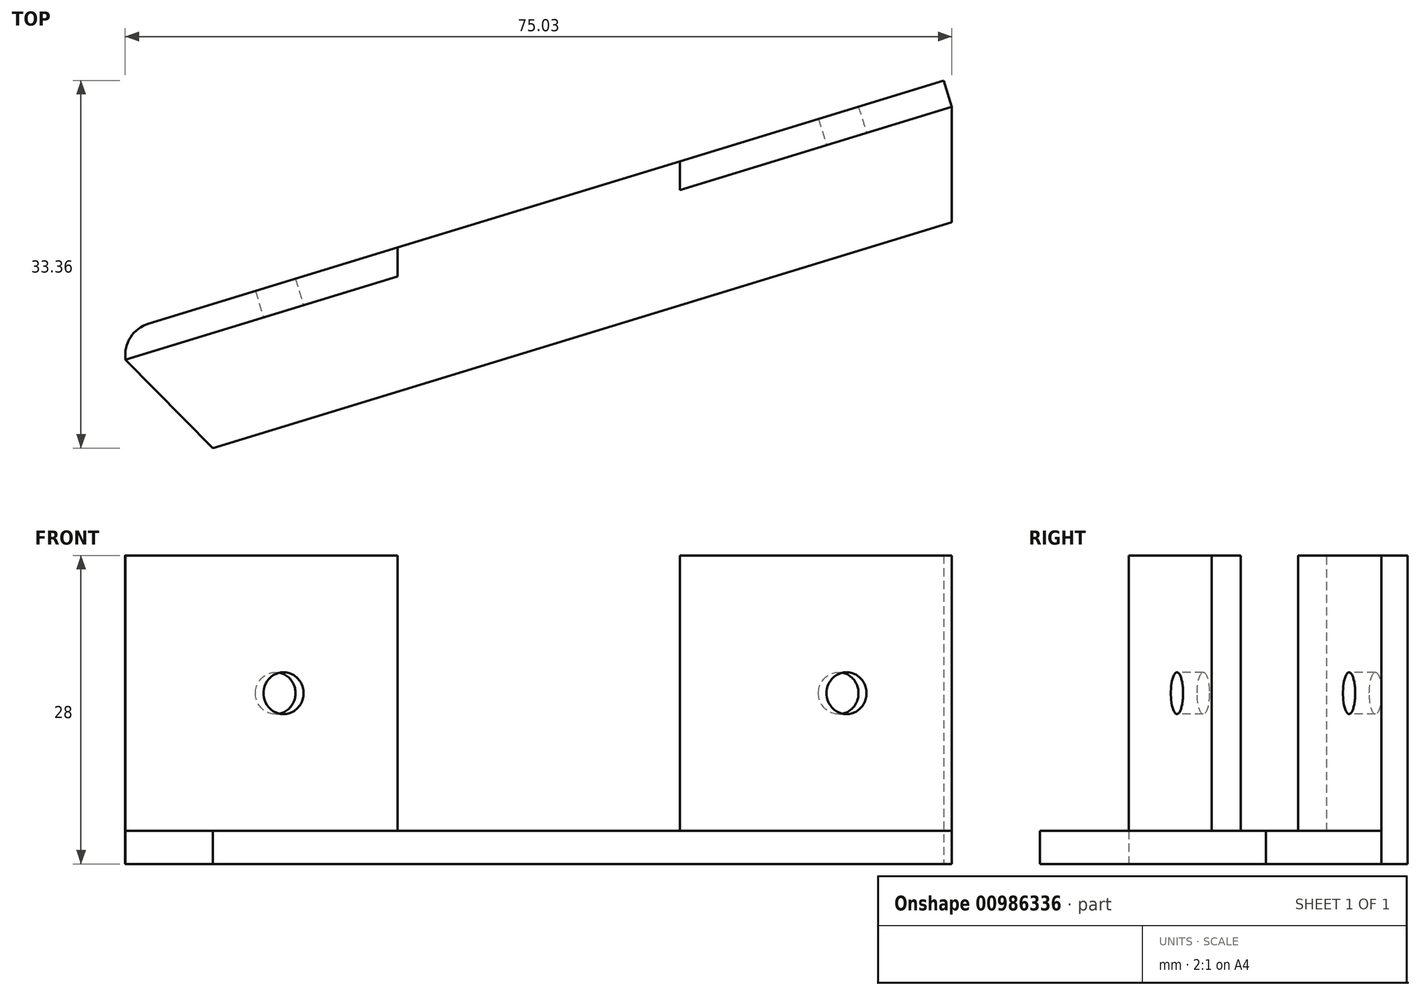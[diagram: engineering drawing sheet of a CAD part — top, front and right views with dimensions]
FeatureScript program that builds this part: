
annotation { "Feature Type Name" : "Feature", "Feature Type Description" : "" }
export const myFeature = defineFeature(function(context is Context, id is Id, definition is map)
    precondition{}
    {
        {
            var Q0;
            Q0=qCreatedBy(makeId("Top.planeOp"),FACE);
            var sketch = newSketch(context, id + "F0", { "sketchPlane" : qUnion([Q0])});
            skLineSegment(sketch, "E0.bottom", {"start": v(0, 0) * mm, "end": v(50, 0) * mm});
            skLineSegment(sketch, "E0.top", {"start": v(0, 33) * mm, "end": v(50, 33) * mm});
            skLineSegment(sketch, "E0.left", {"start": v(0, 0) * mm, "end": v(0, 33) * mm});
            skLineSegment(sketch, "E0.right", {"start": v(50, 0) * mm, "end": v(50, 33) * mm});
            skLineSegment(sketch, "E1", {"start": v(0, 33) * mm, "end": v(50, 48.29) * mm});
            skLineSegment(sketch, "E2", {"start": v(50, 33) * mm, "end": v(50, 48.29) * mm});
            skLineSegment(sketch, "E3", {"start": v(0, 33) * mm, "end": v(-25, 25.36) * mm});
            skLineSegment(sketch, "E4", {"start": v(-25, 25.36) * mm, "end": v(0, 0) * mm});
            skLineSegment(sketch, "E5", {"start": v(0, 33) * mm, "end": v(0, 137) * mm});
            skLineSegment(sketch, "E6", {"start": v(0, 137) * mm, "end": v(25, 137) * mm});
            skLineSegment(sketch, "E7", {"start": v(25, 137) * mm, "end": v(25, 0) * mm});
            skLineSegment(sketch, "E8", {"start": v(0, 137) * mm, "end": v(-25, 131.69) * mm});
            skLineSegment(sketch, "E9", {"start": v(-25, 131.69) * mm, "end": v(-25, 92.43) * mm});
            skLineSegment(sketch, "E10", {"start": v(-25, 131.69) * mm, "end": v(0, 101.46) * mm});
            skLineSegment(sketch, "E11", {"start": v(0, 137) * mm, "end": v(50, 147.63) * mm});
            skLineSegment(sketch, "E12", {"start": v(50, 147.63) * mm, "end": v(50, 131.69) * mm});
            skLineSegment(sketch, "E13", {"start": v(25, 101.46) * mm, "end": v(50, 131.69) * mm});
            skLineSegment(sketch, "E14", {"start": v(0, 137) * mm, "end": v(0, 177) * mm});
            skLineSegment(sketch, "E15", {"start": v(0, 177) * mm, "end": v(25, 177) * mm});
            skPoint(sketch, "E15.endSnap0", {"position": v(25, 142.31) * mm});
            skLineSegment(sketch, "E16", {"start": v(25, 177) * mm, "end": v(25, 137) * mm});
            skSolve(sketch);
        }
        {
            var Q0;
            Q0=qSketchRegion(id+"F0",true);
            extrude(context, id + "F1", {"entities" : qUnion([Q0]), "depth" : 25 * mm});
        }
        {
            var Q0;
            Q0=makeQuery(id+"F1.opExtrude","CAP_FACE",FACE,{"disambiguationData":[OSD([sQuery(id+"F0.wireOp",EDGE,"E0.bottom"),sQuery(id+"F0.wireOp",EDGE,"E0.right"),sQuery(id+"F0.wireOp",EDGE,"E1"),sQuery(id+"F0.wireOp",EDGE,"E2"),sQuery(id+"F0.wireOp",EDGE,"E3"),sQuery(id+"F0.wireOp",EDGE,"E4"),sQuery(id+"F0.wireOp",EDGE,"E5"),sQuery(id+"F0.wireOp",EDGE,"E7"),sQuery(id+"F0.wireOp",EDGE,"E8"),sQuery(id+"F0.wireOp",EDGE,"E10"),sQuery(id+"F0.wireOp",EDGE,"E11"),sQuery(id+"F0.wireOp",EDGE,"E12"),sQuery(id+"F0.wireOp",EDGE,"E13"),sQuery(id+"F0.wireOp",EDGE,"E14"),sQuery(id+"F0.wireOp",EDGE,"E15"),sQuery(id+"F0.wireOp",EDGE,"E16")])],"isStart":true});
            var sketch = newSketch(context, id + "F2", { "sketchPlane" : qUnion([Q0])});
            skLineSegment(sketch, "E17", {"start": v(25, -101.46) * mm, "end": v(0, -101.46) * mm});
            skLineSegment(sketch, "E18", {"start": v(0, -101.46) * mm, "end": v(-25, -131.69) * mm});
            skLineSegment(sketch, "E19", {"start": v(-25, -131.69) * mm, "end": v(50, -147.63) * mm});
            skLineSegment(sketch, "E20", {"start": v(50, -147.63) * mm, "end": v(50, -131.69) * mm});
            skLineSegment(sketch, "E21", {"start": v(50, -131.69) * mm, "end": v(25, -101.46) * mm});
            skSolve(sketch);
        }
        {
            var Q0;
            Q0=qSketchRegion(id+"F2",true);
            extrude(context, id + "F3", {"entities" : qUnion([Q0]), "operationType" : NewBodyOperationType.ADD, "depth" : 10 * mm});
        }
        {
            var Q0;
            Q0=makeQuery(id+"F1.opExtrude","SWEPT_FACE",FACE,{"disambiguationData":[OSD([sQuery(id+"F0.wireOp",EDGE,"E7")])]});
            var sketch = newSketch(context, id + "F4", { "sketchPlane" : qUnion([Q0])});
            skLineSegment(sketch, "E22", {"start": v(147.63, -10) * mm, "end": v(101.46, 0) * mm});
            skLineSegment(sketch, "E23", {"start": v(101.46, 0) * mm, "end": v(101.46, -21.14) * mm});
            skLineSegment(sketch, "E24", {"start": v(101.46, -21.14) * mm, "end": v(147.63, -10) * mm});
            skSolve(sketch);
        }
        {
            var Q0;
            Q0=qSketchRegion(id+"F4",true);
            extrude(context, id + "F5", {"entities" : qUnion([Q0]), "operationType" : NewBodyOperationType.REMOVE, "oppositeDirection" : true, "depth" : 163.4 * mm, "symmetric" : true});
        }
        {
            var Q0;
            {var subQ0=sQuery(id+"F0.wireOp",EDGE,"E13");var subQ1=sQuery(id+"F0.wireOp",EDGE,"E7");var subQ2=sQuery(id+"F0.wireOp",EDGE,"E5");var subQ3=sQuery(id+"F0.wireOp",EDGE,"E4");var subQ4=sQuery(id+"F0.wireOp",EDGE,"E0.bottom");var subQ5=sQuery(id+"F0.wireOp",EDGE,"E10");var subQ6=sQuery(id+"F0.wireOp",EDGE,"E2");var subQ7=sQuery(id+"F0.wireOp",EDGE,"E0.right");var subQ8=sQuery(id+"F0.wireOp",EDGE,"E1");var subQ9=sQuery(id+"F0.wireOp",EDGE,"E3");Q0=makeQuery(id+"F3.boolean.opBoolean","SPLIT",FACE,{"disambiguationData":[TD([makeQuery(id+"F1.opExtrude","SWEPT_FACE",FACE,{"disambiguationData":[OSD([subQ4])]})])],"derivedFrom":makeQuery(id+"F1.opExtrude","CAP_FACE",FACE,{"disambiguationData":[OSD([subQ4,subQ7,subQ8,subQ6,subQ9,subQ3,subQ2,subQ1,sQuery(id+"F0.wireOp",EDGE,"E8"),subQ5,sQuery(id+"F0.wireOp",EDGE,"E11"),sQuery(id+"F0.wireOp",EDGE,"E12"),subQ0,sQuery(id+"F0.wireOp",EDGE,"E14"),sQuery(id+"F0.wireOp",EDGE,"E15"),sQuery(id+"F0.wireOp",EDGE,"E16")])],"isStart":true})});}
            var sketch = newSketch(context, id + "F6", { "sketchPlane" : qUnion([Q0])});
            skLineSegment(sketch, "E25", {"start": v(50, 0) * mm, "end": v(50, -48.29) * mm});
            skLineSegment(sketch, "E26", {"start": v(50, -48.29) * mm, "end": v(-25, -25.36) * mm});
            skLineSegment(sketch, "E27", {"start": v(-25, -25.36) * mm, "end": v(0, 0) * mm});
            skLineSegment(sketch, "E28", {"start": v(0, 0) * mm, "end": v(50, 0) * mm});
            skSolve(sketch);
        }
        {
            var Q0;
            Q0=qSketchRegion(id+"F6",true);
            extrude(context, id + "F7", {"entities" : qUnion([Q0]), "operationType" : NewBodyOperationType.ADD, "depth" : 10 * mm});
        }
        {
            var Q0;
            Q0=makeQuery(id+"F7.boolean.opBoolean","MERGE",FACE,{"derivedFrom":[makeQuery(id+"F1.opExtrude","SWEPT_FACE",FACE,{"disambiguationData":[OSD([sQuery(id+"F0.wireOp",EDGE,"E0.right"),sQuery(id+"F0.wireOp",EDGE,"E2")])]}),makeQuery(id+"F7.opExtrude","SWEPT_FACE",FACE,{"disambiguationData":[OSD([sQuery(id+"F6.wireOp",EDGE,"E25")])]})]});
            var sketch = newSketch(context, id + "F8", { "sketchPlane" : qUnion([Q0])});
            skLineSegment(sketch, "E29", {"start": v(0, 0) * mm, "end": v(48.29, -10) * mm});
            skLineSegment(sketch, "E30", {"start": v(48.29, -10) * mm, "end": v(48.29, -39.53) * mm});
            skLineSegment(sketch, "E31", {"start": v(48.29, -39.53) * mm, "end": v(0, -39.53) * mm});
            skLineSegment(sketch, "E32", {"start": v(0, -39.53) * mm, "end": v(0, 0) * mm});
            skSolve(sketch);
        }
        {
            var Q0;
            Q0=qSketchRegion(id+"F8",true);
            extrude(context, id + "F9", {"entities" : qUnion([Q0]), "operationType" : NewBodyOperationType.REMOVE, "oppositeDirection" : true, "depth" : 92 * mm});
        }
        {
            var Q0;
            Q0=makeQuery(id+"F1.opExtrude","SWEPT_FACE",FACE,{"disambiguationData":[OSD([sQuery(id+"F0.wireOp",EDGE,"E15")])]});
            var sketch = newSketch(context, id + "F10", { "sketchPlane" : qUnion([Q0])});
            skLineSegment(sketch, "E33.bottom", {"start": v(-6, 19) * mm, "end": v(-19, 19) * mm});
            skLineSegment(sketch, "E33.top", {"start": v(-6, 6) * mm, "end": v(-19, 6) * mm});
            skLineSegment(sketch, "E33.left", {"start": v(-6, 19) * mm, "end": v(-6, 6) * mm});
            skLineSegment(sketch, "E33.right", {"start": v(-19, 19) * mm, "end": v(-19, 6) * mm});
            skPoint(sketch, "E33.middle", {"position": v(-12.5, 12.5) * mm});
            skPoint(sketch, "E33.middle.positionSnap0", {"position": v(-25, 12.5) * mm});
            skPoint(sketch, "E33.middle.positionSnap1", {"position": v(-12.5, 25) * mm});
            skPoint(sketch, "E33.centerSnap0", {"position": v(-25, 12.5) * mm});
            skPoint(sketch, "E33.centerSnap1", {"position": v(-12.5, 25) * mm});
            skSolve(sketch);
        }
        {
            var Q0;
            Q0=qSketchRegion(id+"F10",true);
            extrude(context, id + "F11", {"entities" : qUnion([Q0]), "operationType" : NewBodyOperationType.REMOVE, "oppositeDirection" : true, "depth" : 40 * mm});
        }
        {
            var Q0;
            Q0=makeQuery(id+"F3.boolean.opBoolean","MERGE",FACE,{"derivedFrom":[makeQuery(id+"F1.opExtrude","SWEPT_FACE",FACE,{"disambiguationData":[OSD([sQuery(id+"F0.wireOp",EDGE,"E8")])]}),makeQuery(id+"F1.opExtrude","SWEPT_FACE",FACE,{"disambiguationData":[OSD([sQuery(id+"F0.wireOp",EDGE,"E11")])]}),makeQuery(id+"F3.opExtrude","SWEPT_FACE",FACE,{"disambiguationData":[OSD([sQuery(id+"F2.wireOp",EDGE,"E19")])]})]});
            var sketch = newSketch(context, id + "F12", { "sketchPlane" : qUnion([Q0])});
            skLineSegment(sketch, "E34", {"start": v(-2.93, 25) * mm, "end": v(-2.93, 12.5) * mm});
            skPoint(sketch, "E34.endSnap0", {"position": v(-28.48, 12.5) * mm});
            skLineSegment(sketch, "E35", {"start": v(-2.93, 12.5) * mm, "end": v(-18.63, 12.5) * mm});
            skCircle(sketch, "E36", {"center": v(-18.63, 12.5) * mm, "radius": 1.9 * mm});
            skLineSegment(sketch, "E37", {"start": v(-79.6, 25) * mm, "end": v(-79.6, 12.5) * mm});
            skLineSegment(sketch, "E38", {"start": v(-79.6, 12.5) * mm, "end": v(-70.3, 12.5) * mm});
            skCircle(sketch, "E39", {"center": v(-70.3, 12.5) * mm, "radius": 1.9 * mm});
            skSolve(sketch);
        }
        {
            var Q0;
            Q0=qSketchRegion(id+"F12",true);
            extrude(context, id + "F13", {"entities" : qUnion([Q0]), "operationType" : NewBodyOperationType.REMOVE, "oppositeDirection" : true, "depth" : 7 * mm});
        }
        {
            var Q0;
            Q0=makeQuery(id+"F7.boolean.opBoolean","MERGE",FACE,{"derivedFrom":[makeQuery(id+"F1.opExtrude","SWEPT_FACE",FACE,{"disambiguationData":[OSD([sQuery(id+"F0.wireOp",EDGE,"E1")])]}),makeQuery(id+"F1.opExtrude","SWEPT_FACE",FACE,{"disambiguationData":[OSD([sQuery(id+"F0.wireOp",EDGE,"E3")])]}),makeQuery(id+"F7.opExtrude","SWEPT_FACE",FACE,{"disambiguationData":[OSD([sQuery(id+"F6.wireOp",EDGE,"E26")])]})]});
            cPlane(context, id + "F14", {"entities" : qUnion([Q0]), "cplaneType" : CPlaneType.OFFSET, "offset" : 0 * mm, "width" : 150 * mm, "height" : 150 * mm});
        }
        {
            var Q0;
            Q0=makeQuery(id+"F7.boolean.opBoolean","MERGE",FACE,{"derivedFrom":[makeQuery(id+"F1.opExtrude","SWEPT_FACE",FACE,{"disambiguationData":[OSD([sQuery(id+"F0.wireOp",EDGE,"E1")])]}),makeQuery(id+"F1.opExtrude","SWEPT_FACE",FACE,{"disambiguationData":[OSD([sQuery(id+"F0.wireOp",EDGE,"E3")])]}),makeQuery(id+"F7.opExtrude","SWEPT_FACE",FACE,{"disambiguationData":[OSD([sQuery(id+"F6.wireOp",EDGE,"E26")])]})]});
            extrude(context, id + "F15", {"entities" : qUnion([Q0]), "operationType" : NewBodyOperationType.ADD, "depth" : 2.5 * mm});
        }
        {
            var Q0;
            Q0=makeQuery(id+"F15.opExtrude","CAP_FACE",FACE,{"disambiguationData":[OSD([sQuery(id+"F0.wireOp",EDGE,"E1"),sQuery(id+"F0.wireOp",EDGE,"E3"),sQuery(id+"F6.wireOp",EDGE,"E26")])],"isStart":false});
            var sketch = newSketch(context, id + "F16", { "sketchPlane" : qUnion([Q0])});
            skLineSegment(sketch, "E40.bottom", {"start": v(16.5, 25) * mm, "end": v(-61.93, 25) * mm});
            skLineSegment(sketch, "E40.top", {"start": v(16.5, 0) * mm, "end": v(-61.93, 0) * mm});
            skLineSegment(sketch, "E40.left", {"start": v(16.5, 25) * mm, "end": v(16.5, 0) * mm});
            skLineSegment(sketch, "E40.right", {"start": v(-61.93, 25) * mm, "end": v(-61.93, 0) * mm});
            skSolve(sketch);
        }
        {
            var Q0;
            Q0=qSketchRegion(id+"F16",true);
            extrude(context, id + "F17", {"entities" : qUnion([Q0]), "operationType" : NewBodyOperationType.ADD, "oppositeDirection" : true, "depth" : 2.5 * mm});
        }
        {
            var Q0;
            Q0=makeQuery(id+"F17.boolean.opBoolean","MERGE",FACE,{"derivedFrom":[makeQuery(id+"F15.opExtrude","CAP_FACE",FACE,{"disambiguationData":[OSD([sQuery(id+"F0.wireOp",EDGE,"E1"),sQuery(id+"F0.wireOp",EDGE,"E3"),sQuery(id+"F6.wireOp",EDGE,"E26")])],"isStart":false}),makeQuery(id+"F17.opExtrude","CAP_FACE",FACE,{"disambiguationData":[OSD([sQuery(id+"F16.wireOp",EDGE,"E40.bottom"),sQuery(id+"F16.wireOp",EDGE,"E40.top"),sQuery(id+"F16.wireOp",EDGE,"E40.left"),sQuery(id+"F16.wireOp",EDGE,"E40.right")])],"isStart":true})]});
            var sketch = newSketch(context, id + "F18", { "sketchPlane" : qUnion([Q0])});
            skLineSegment(sketch, "E41.top", {"start": v(16.5, -3) * mm, "end": v(-61.93, -3) * mm});
            skLineSegment(sketch, "E42.bottom", {"start": v(16.5, -3) * mm, "end": v(-74.36, -3) * mm});
            skLineSegment(sketch, "E42.top", {"start": v(16.5, -15.71) * mm, "end": v(-74.36, -15.71) * mm});
            skLineSegment(sketch, "E42.left", {"start": v(16.5, -3) * mm, "end": v(16.5, -15.71) * mm});
            skLineSegment(sketch, "E42.right", {"start": v(-74.36, -3) * mm, "end": v(-74.36, -15.71) * mm});
            skSolve(sketch);
        }
        {
            var Q0;
            Q0=qSketchRegion(id+"F18",true);
            extrude(context, id + "F19", {"entities" : qUnion([Q0]), "operationType" : NewBodyOperationType.REMOVE, "oppositeDirection" : true, "depth" : 336 * mm});
        }
        {
            var Q0;
            {var subQ0=sQuery(id+"F0.wireOp",EDGE,"E3");var subQ1=sQuery(id+"F0.wireOp",EDGE,"E1");Q0=makeQuery(id+"F17.boolean.opBoolean","MERGE",FACE,{"derivedFrom":[makeQuery(id+"F15.boolean.opBoolean","MERGE",FACE,{"derivedFrom":[makeQuery(id+"F1.opExtrude","CAP_FACE",FACE,{"disambiguationData":[OSD([sQuery(id+"F0.wireOp",EDGE,"E0.bottom"),sQuery(id+"F0.wireOp",EDGE,"E0.right"),subQ1,sQuery(id+"F0.wireOp",EDGE,"E2"),subQ0,sQuery(id+"F0.wireOp",EDGE,"E4"),sQuery(id+"F0.wireOp",EDGE,"E5"),sQuery(id+"F0.wireOp",EDGE,"E7"),sQuery(id+"F0.wireOp",EDGE,"E8"),sQuery(id+"F0.wireOp",EDGE,"E10"),sQuery(id+"F0.wireOp",EDGE,"E11"),sQuery(id+"F0.wireOp",EDGE,"E12"),sQuery(id+"F0.wireOp",EDGE,"E13"),sQuery(id+"F0.wireOp",EDGE,"E14"),sQuery(id+"F0.wireOp",EDGE,"E15"),sQuery(id+"F0.wireOp",EDGE,"E16")])],"isStart":false}),makeQuery(id+"F15.opExtrude","SWEPT_FACE",FACE,{"disambiguationData":[OSD([subQ1])]}),makeQuery(id+"F15.opExtrude","SWEPT_FACE",FACE,{"disambiguationData":[OSD([subQ0])]})]}),makeQuery(id+"F17.opExtrude","SWEPT_FACE",FACE,{"disambiguationData":[OSD([sQuery(id+"F16.wireOp",EDGE,"E40.bottom")])]})]});}
            var sketch = newSketch(context, id + "F20", { "sketchPlane" : qUnion([Q0])});
            skLineSegment(sketch, "E43", {"start": v(-25, 25.36) * mm, "end": v(50, 48.29) * mm});
            skLineSegment(sketch, "E44", {"start": v(50, 48.29) * mm, "end": v(63.77, -9.77) * mm});
            skLineSegment(sketch, "E45", {"start": v(63.77, -9.77) * mm, "end": v(-20.6, -5.85) * mm});
            skLineSegment(sketch, "E46", {"start": v(-20.6, -5.85) * mm, "end": v(-25, 25.36) * mm});
            skSolve(sketch);
        }
        {
            var Q0;
            Q0=qSketchRegion(id+"F20",true);
            extrude(context, id + "F21", {"entities" : qUnion([Q0]), "operationType" : NewBodyOperationType.REMOVE, "oppositeDirection" : true, "depth" : 25 * mm});
        }
        {
            var Q0;
            Q0=qCreatedBy(id+"F14.planeOp",FACE);
            cPlane(context, id + "F22", {"entities" : qUnion([Q0]), "cplaneType" : CPlaneType.OFFSET, "offset" : 10 * mm, "oppositeDirection" : true, "width" : 150 * mm, "height" : 150 * mm});
        }
        {
            var Q0;
            Q0=qCreatedBy(id+"F22.planeOp",FACE);
            var sketch = newSketch(context, id + "F23", { "sketchPlane" : qUnion([Q0])});
            skLineSegment(sketch, "E47.bottom", {"start": v(-66.06, 2.6) * mm, "end": v(24.9, 2.6) * mm});
            skLineSegment(sketch, "E47.top", {"start": v(-66.06, -7.75) * mm, "end": v(24.9, -7.75) * mm});
            skLineSegment(sketch, "E47.left", {"start": v(-66.06, 2.6) * mm, "end": v(-66.06, -7.75) * mm});
            skLineSegment(sketch, "E47.right", {"start": v(24.9, 2.6) * mm, "end": v(24.9, -7.75) * mm});
            skSolve(sketch);
        }
        {
            var Q0;
            Q0=qSketchRegion(id+"F23",true);
            extrude(context, id + "F24", {"entities" : qUnion([Q0]), "operationType" : NewBodyOperationType.REMOVE, "oppositeDirection" : true, "depth" : 48.1 * mm});
        }
        {
            var Q0;
            Q0=makeQuery(id+"F1.opExtrude","SWEPT_FACE",FACE,{"disambiguationData":[OSD([sQuery(id+"F0.wireOp",EDGE,"E15")])]});
            var sketch = newSketch(context, id + "F25", { "sketchPlane" : qUnion([Q0])});
            skLineSegment(sketch, "E48.bottom", {"start": v(0, 25) * mm, "end": v(-25, 25) * mm});
            skLineSegment(sketch, "E48.top", {"start": v(0, 0) * mm, "end": v(-25, 0) * mm});
            skLineSegment(sketch, "E49.bottom", {"start": v(-25, 0) * mm, "end": v(-25.3, 0) * mm});
            skLineSegment(sketch, "E49.top", {"start": v(-25, 25) * mm, "end": v(-25.3, 25) * mm});
            skLineSegment(sketch, "E49.right", {"start": v(-25.3, 0) * mm, "end": v(-25.3, 25) * mm});
            skLineSegment(sketch, "E50.bottom", {"start": v(0, 25) * mm, "end": v(0.3, 25) * mm});
            skLineSegment(sketch, "E50.top", {"start": v(0, 0) * mm, "end": v(0.3, 0) * mm});
            skLineSegment(sketch, "E50.right", {"start": v(0.3, 25) * mm, "end": v(0.3, 0) * mm});
            skSolve(sketch);
        }
        {
            var Q0;
            Q0=qSketchRegion(id+"F25",true);
            extrude(context, id + "F26", {"entities" : qUnion([Q0]), "operationType" : NewBodyOperationType.REMOVE, "oppositeDirection" : true, "depth" : 199 * mm});
        }
        {
            var Q0;
            Q0=makeQuery(id+"F17.boolean.opBoolean","MERGE",FACE,{"derivedFrom":[makeQuery(id+"F15.opExtrude","CAP_FACE",FACE,{"disambiguationData":[OSD([sQuery(id+"F0.wireOp",EDGE,"E1"),sQuery(id+"F0.wireOp",EDGE,"E3"),sQuery(id+"F6.wireOp",EDGE,"E26")])],"isStart":false}),makeQuery(id+"F17.opExtrude","CAP_FACE",FACE,{"disambiguationData":[OSD([sQuery(id+"F16.wireOp",EDGE,"E40.bottom"),sQuery(id+"F16.wireOp",EDGE,"E40.top"),sQuery(id+"F16.wireOp",EDGE,"E40.left"),sQuery(id+"F16.wireOp",EDGE,"E40.right")])],"isStart":true})]});
            var sketch = newSketch(context, id + "F27", { "sketchPlane" : qUnion([Q0])});
            skLineSegment(sketch, "E51.bottom", {"start": v(40.08, -30.15) * mm, "end": v(-143.24, -30.15) * mm});
            skLineSegment(sketch, "E51.top", {"start": v(40.08, 53.76) * mm, "end": v(-143.24, 53.76) * mm});
            skLineSegment(sketch, "E51.left", {"start": v(40.08, -30.15) * mm, "end": v(40.08, 53.76) * mm});
            skLineSegment(sketch, "E51.right", {"start": v(-143.24, -30.15) * mm, "end": v(-143.24, 53.76) * mm});
            skSolve(sketch);
        }
        {
            var Q0;
            Q0=qSketchRegion(id+"F27",true);
            extrude(context, id + "F28", {"entities" : qUnion([Q0]), "operationType" : NewBodyOperationType.REMOVE, "depth" : 179 * mm});
        }
        {
            var Q0;
            Q0=makeQuery(id+"F15.opExtrude","CAP_EDGE",EDGE,{"disambiguationData":[OSD([sQuery(id+"F0.wireOp",EDGE,"E3"),sQuery(id+"F0.wireOp",EDGE,"E4"),sQuery(id+"F6.wireOp",EDGE,"E26"),sQuery(id+"F6.wireOp",EDGE,"E27")])],"isStart":false});
            fillet(context, id + "F29", {"entities" : qUnion([Q0]), "radius" : 3 * mm, "tangentPropagation" : true, "allowEdgeOverflow" : false});
        }
        {
            var Q0;
            {var subQ2=sQuery(id+"F0.wireOp",EDGE,"E4");var subQ4=sQuery(id+"F20.wireOp",EDGE,"E43");Q0=makeQuery(id+"F26.boolean.opBoolean","SPLIT",FACE,{"disambiguationData":[TD([makeQuery(id+"F1.opExtrude","SWEPT_FACE",FACE,{"disambiguationData":[OSD([subQ2])]})])],"derivedFrom":makeQuery(id+"F21.boolean.opBoolean","COPY",FACE,{"derivedFrom":makeQuery(id+"F21.opExtrude","SWEPT_FACE",FACE,{"disambiguationData":[OSD([subQ4])]})})});}
            var sketch = newSketch(context, id + "F30", { "sketchPlane" : qUnion([Q0])});
            skLineSegment(sketch, "E52", {"start": v(-16.5, 25) * mm, "end": v(-16.5, 12.5) * mm});
            skLineSegment(sketch, "E53", {"start": v(-16.5, 12.5) * mm, "end": v(-1.5, 12.5) * mm});
            skCircle(sketch, "E54", {"center": v(-1.5, 12.5) * mm, "radius": 1.9 * mm});
            skSolve(sketch);
        }
        {
            var Q0;
            Q0=qSketchRegion(id+"F30",true);
            extrude(context, id + "F31", {"entities" : qUnion([Q0]), "operationType" : NewBodyOperationType.REMOVE, "oppositeDirection" : true, "depth" : 25 * mm});
        }
        {
            var Q0;
            {var subQ3=sQuery(id+"F6.wireOp",EDGE,"E25");var subQ5=sQuery(id+"F20.wireOp",EDGE,"E43");Q0=makeQuery(id+"F26.boolean.opBoolean","SPLIT",FACE,{"disambiguationData":[TD([makeQuery(id+"F7.opExtrude","SWEPT_FACE",FACE,{"disambiguationData":[OSD([subQ3])]})])],"derivedFrom":makeQuery(id+"F21.boolean.opBoolean","COPY",FACE,{"derivedFrom":makeQuery(id+"F21.opExtrude","SWEPT_FACE",FACE,{"disambiguationData":[OSD([subQ5])]})})});}
            var sketch = newSketch(context, id + "F32", { "sketchPlane" : qUnion([Q0])});
            skLineSegment(sketch, "E55", {"start": v(61.93, 25) * mm, "end": v(61.93, 12.5) * mm});
            skLineSegment(sketch, "E56", {"start": v(61.93, 12.5) * mm, "end": v(51.93, 12.5) * mm});
            skCircle(sketch, "E57", {"center": v(51.93, 12.5) * mm, "radius": 1.9 * mm});
            skSolve(sketch);
        }
        {
            var Q0;
            Q0=qSketchRegion(id+"F32",true);
            extrude(context, id + "F33", {"entities" : qUnion([Q0]), "operationType" : NewBodyOperationType.REMOVE, "oppositeDirection" : true, "depth" : 25 * mm});
        }
    });
